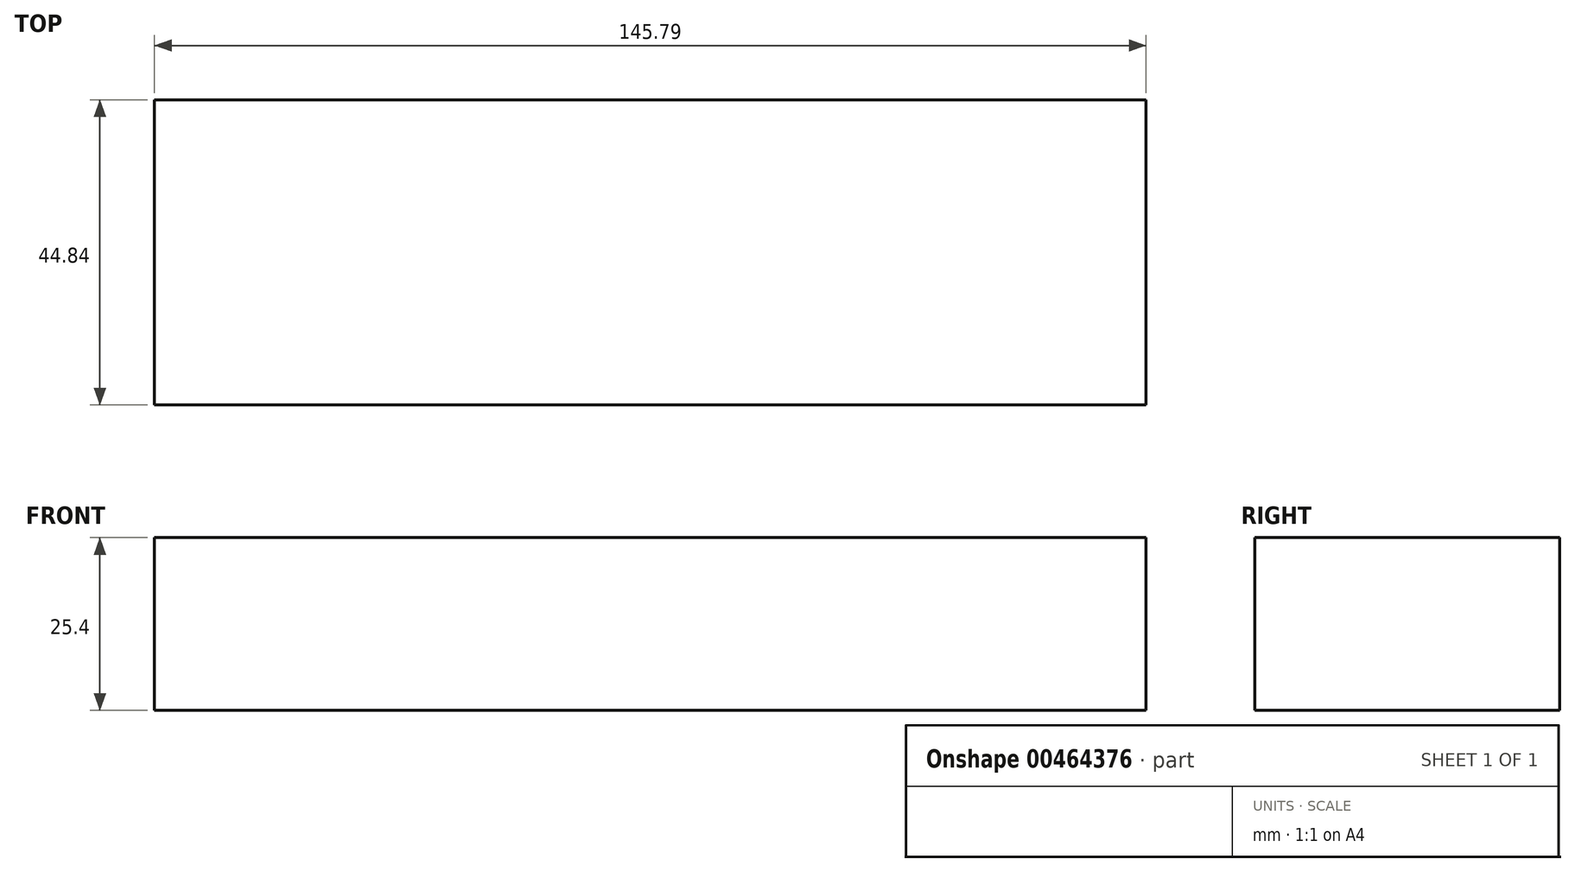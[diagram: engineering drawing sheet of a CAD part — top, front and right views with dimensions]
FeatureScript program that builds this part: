
annotation { "Feature Type Name" : "Feature", "Feature Type Description" : "" }
export const myFeature = defineFeature(function(context is Context, id is Id, definition is map)
    precondition{}
    {
        {
            var Q0;
            Q0=qCreatedBy(makeId("Top.planeOp"),FACE);
            var sketch = newSketch(context, id + "F0", { "sketchPlane" : qUnion([Q0])});
            skLineSegment(sketch, "E0.bottom", {"start": v(-72.76, 49.94) * mm, "end": v(73.03, 49.94) * mm});
            skLineSegment(sketch, "E0.top", {"start": v(-72.76, 5.1) * mm, "end": v(73.03, 5.1) * mm});
            skLineSegment(sketch, "E0.left", {"start": v(-72.76, 49.94) * mm, "end": v(-72.76, 5.1) * mm});
            skLineSegment(sketch, "E0.right", {"start": v(73.03, 49.94) * mm, "end": v(73.03, 5.1) * mm});
            skSolve(sketch);
        }
        {
            var Q0;
            Q0=makeQuery(id+"F0.imprint","IMPRINT",FACE,{"disambiguationData":[TD([[makeQuery(id+"F0.imprint","IMPRINT",EDGE,{"derivedFrom":sQuery(id+"F0.wireOp",EDGE,"E0.bottom")}),-1.0]])]});
            extrude(context, id + "F1", {"entities" : qUnion([Q0]), "depth" : 25.4 * mm});
        }
    });
